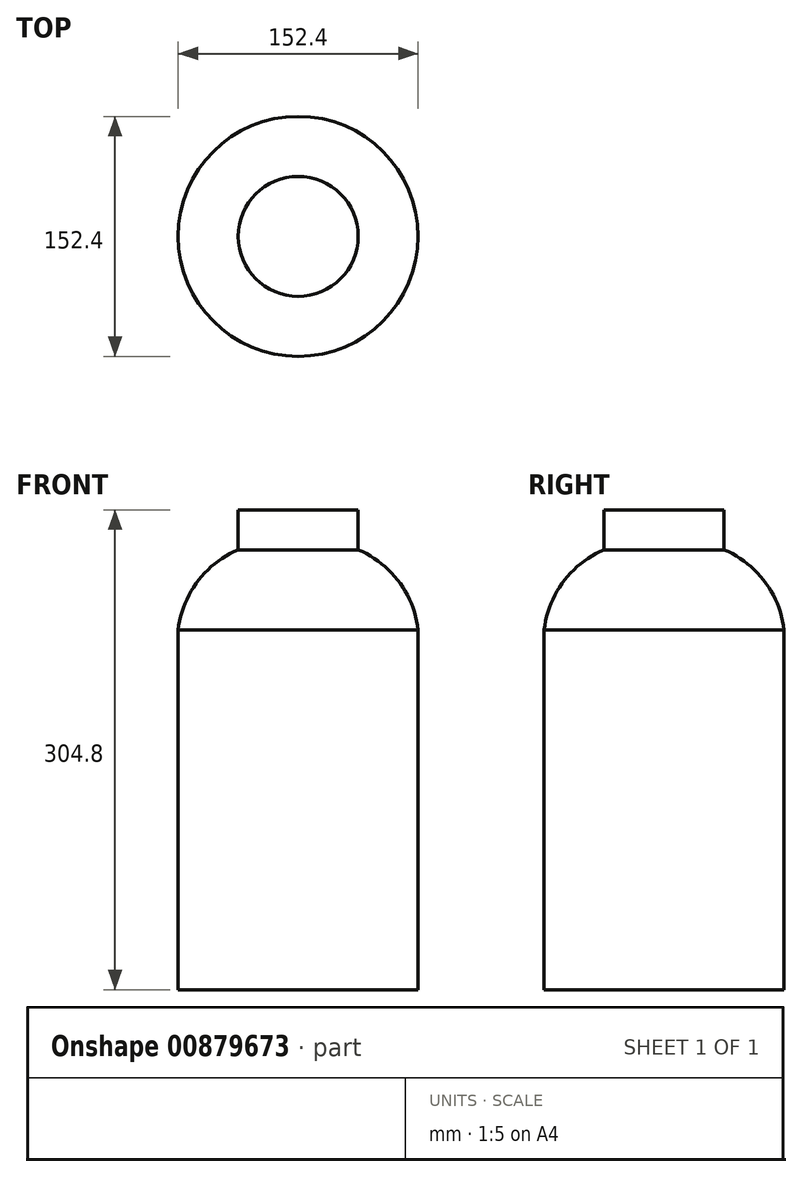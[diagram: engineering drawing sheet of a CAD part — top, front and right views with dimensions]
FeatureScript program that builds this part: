
annotation { "Feature Type Name" : "Feature", "Feature Type Description" : "" }
export const myFeature = defineFeature(function(context is Context, id is Id, definition is map)
    precondition{}
    {
        {
            var Q0;
            Q0=qCreatedBy(makeId("Front.planeOp"),FACE);
            var sketch = newSketch(context, id + "F0", { "sketchPlane" : qUnion([Q0])});
            skLineSegment(sketch, "E0", {"start": v(0, 0) * mm, "end": v(0, 304.8) * mm});
            skLineSegment(sketch, "E1", {"start": v(0, 304.8) * mm, "end": v(38.1, 304.8) * mm});
            skLineSegment(sketch, "E2", {"start": v(38.1, 304.8) * mm, "end": v(38.1, 279.4) * mm});
            skArc(sketch, "E3", {"start": v(76.2, 228.6) * mm, "mid": v(64, 259.14) * mm, "end": v(38.1, 279.4) * mm});
            skLineSegment(sketch, "E4", {"start": v(76.2, 228.6) * mm, "end": v(76.2, 0) * mm});
            skLineSegment(sketch, "E5", {"start": v(76.2, 0) * mm, "end": v(0, 0) * mm});
            skSolve(sketch);
        }
        {
            var Q0;
            Q0=makeQuery(id+"F0.imprint","IMPRINT",FACE,{"disambiguationData":[TD([[makeQuery(id+"F0.imprint","IMPRINT",EDGE,{"derivedFrom":sQuery(id+"F0.wireOp",EDGE,"E0")}),-1.0]])]});
            var Q1;
            Q1=sQuery(id+"F0.wireOp",EDGE,"E0");
            revolve(context, id + "F1", {"surfaceOperationType" : NewSurfaceOperationType.NEW, "entities" : qUnion([Q0]), "axis" : qUnion([Q1]), "revolveType" : RevolveType.FULL});
        }
    });
